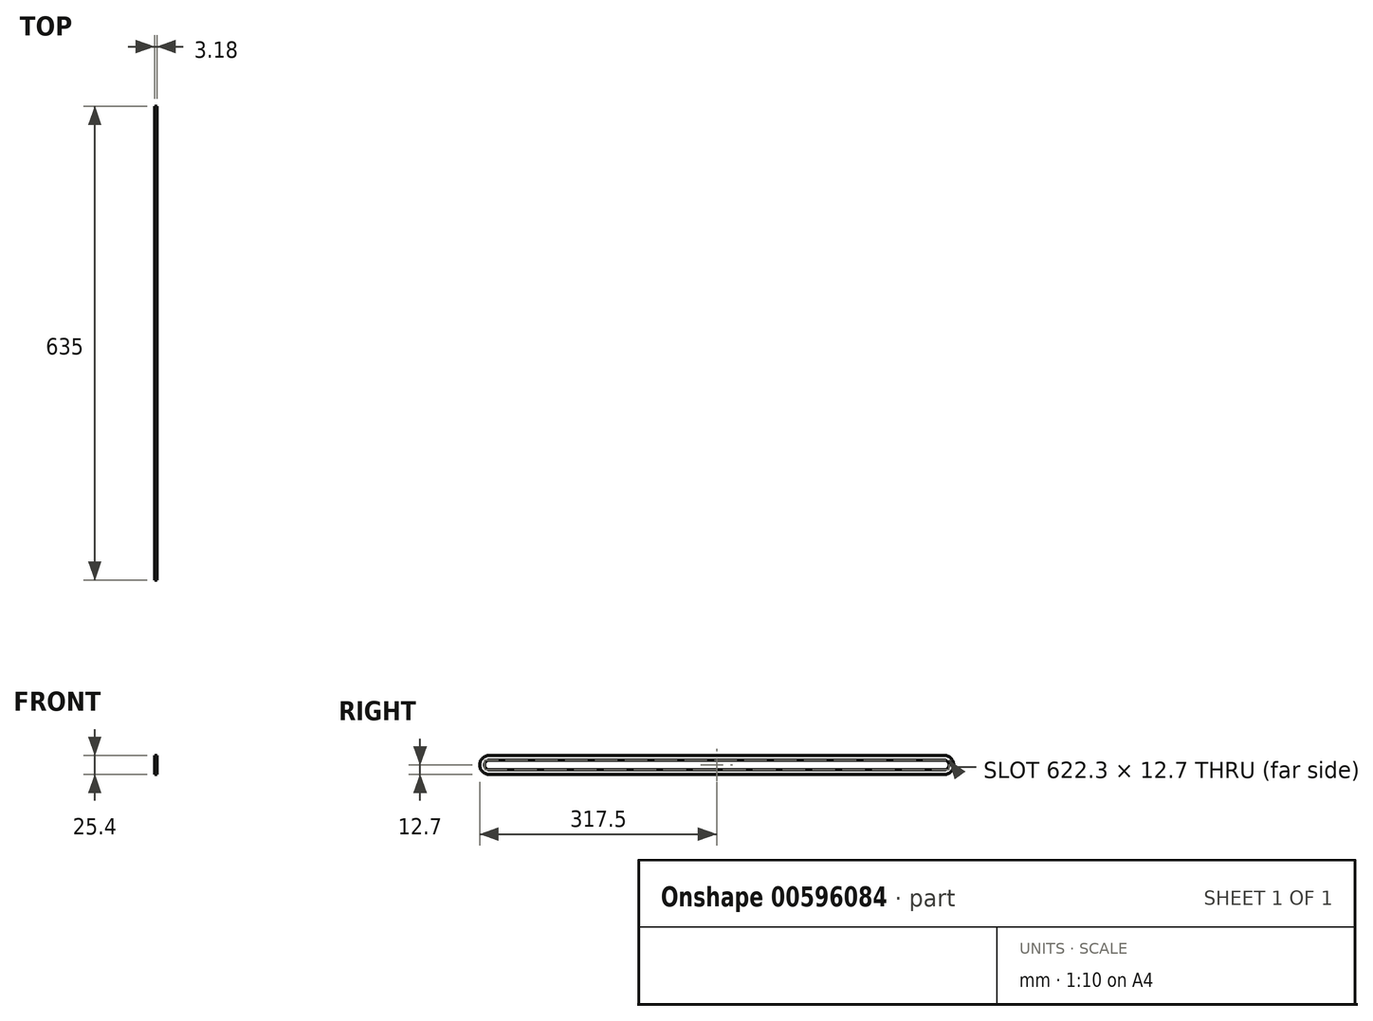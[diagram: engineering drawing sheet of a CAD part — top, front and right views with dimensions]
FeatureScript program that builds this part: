
annotation { "Feature Type Name" : "Feature", "Feature Type Description" : "" }
export const myFeature = defineFeature(function(context is Context, id is Id, definition is map)
    precondition{}
    {
        {
            var Q0;
            Q0=qCreatedBy(makeId("Right.planeOp"),FACE);
            var sketch = newSketch(context, id + "F0", { "sketchPlane" : qUnion([Q0])});
            skCircle(sketch, "E0", {"center": v(0, 0) * mm, "radius": 12.7 * mm, "construction": true});
            skLineSegment(sketch, "E1", {"start": v(0, 12.7) * mm, "end": v(304.8, 12.7) * mm});
            skLineSegment(sketch, "E2", {"start": v(0, -12.7) * mm, "end": v(304.8, -12.7) * mm});
            skArc(sketch, "E3", {"start": v(304.8, 12.7) * mm, "mid": v(317.5, 0) * mm, "end": v(304.8, -12.7) * mm});
            skLineSegment(sketch, "E4.MirrorCS", {"start": v(0, -12.7) * mm, "end": v(-304.8, -12.7) * mm});
            skLineSegment(sketch, "E5.MirrorCS", {"start": v(0, 12.7) * mm, "end": v(-304.8, 12.7) * mm});
            skArc(sketch, "E6.MirrorCS", {"start": v(-304.8, 12.7) * mm, "mid": v(-317.5, 0) * mm, "end": v(-304.8, -12.7) * mm});
            skSolve(sketch);
        }
        {
            var Q0;
            Q0=makeQuery(id+"F0.imprint","IMPRINT",FACE,{"disambiguationData":[TD([[makeQuery(id+"F0.imprint","IMPRINT",EDGE,{"derivedFrom":sQuery(id+"F0.wireOp",EDGE,"E1")}),-1.0]])]});
            extrude(context, id + "F1", {"entities" : qUnion([Q0]), "depth" : 3.17 * mm, "offsetDistance" : 25.4 * mm});
        }
        {
            var Q0;
            Q0=makeQuery(id+"F1.opExtrude","CAP_FACE",FACE,{"disambiguationData":[OSD([sQuery(id+"F0.wireOp",EDGE,"E1"),sQuery(id+"F0.wireOp",EDGE,"E2"),sQuery(id+"F0.wireOp",EDGE,"E3"),sQuery(id+"F0.wireOp",EDGE,"E4.MirrorCS"),sQuery(id+"F0.wireOp",EDGE,"E5.MirrorCS"),sQuery(id+"F0.wireOp",EDGE,"E6.MirrorCS")])],"isStart":false});
            var sketch = newSketch(context, id + "F2", { "sketchPlane" : qUnion([Q0])});
            skLineSegment(sketch, "E7.0", {"start": v(-304.8, -6.35) * mm, "end": v(304.8, -6.35) * mm});
            skArc(sketch, "E7.1", {"start": v(-304.8, 6.35) * mm, "mid": v(-311.15, 0) * mm, "end": v(-304.8, -6.35) * mm});
            skLineSegment(sketch, "E7.2", {"start": v(304.8, 6.35) * mm, "end": v(-304.8, 6.35) * mm});
            skArc(sketch, "E7.3", {"start": v(304.8, -6.35) * mm, "mid": v(311.15, 0) * mm, "end": v(304.8, 6.35) * mm});
            skSolve(sketch);
        }
        {
            var Q0;
            Q0 = qSketchRegion(id + "F2", true);
            extrude(context, id + "F3", {"entities" : qUnion([Q0]), "operationType" : NewBodyOperationType.REMOVE, "oppositeDirection" : true, "depth" : 209.8 * mm, "offsetDistance" : 25.4 * mm});
        }
    });
